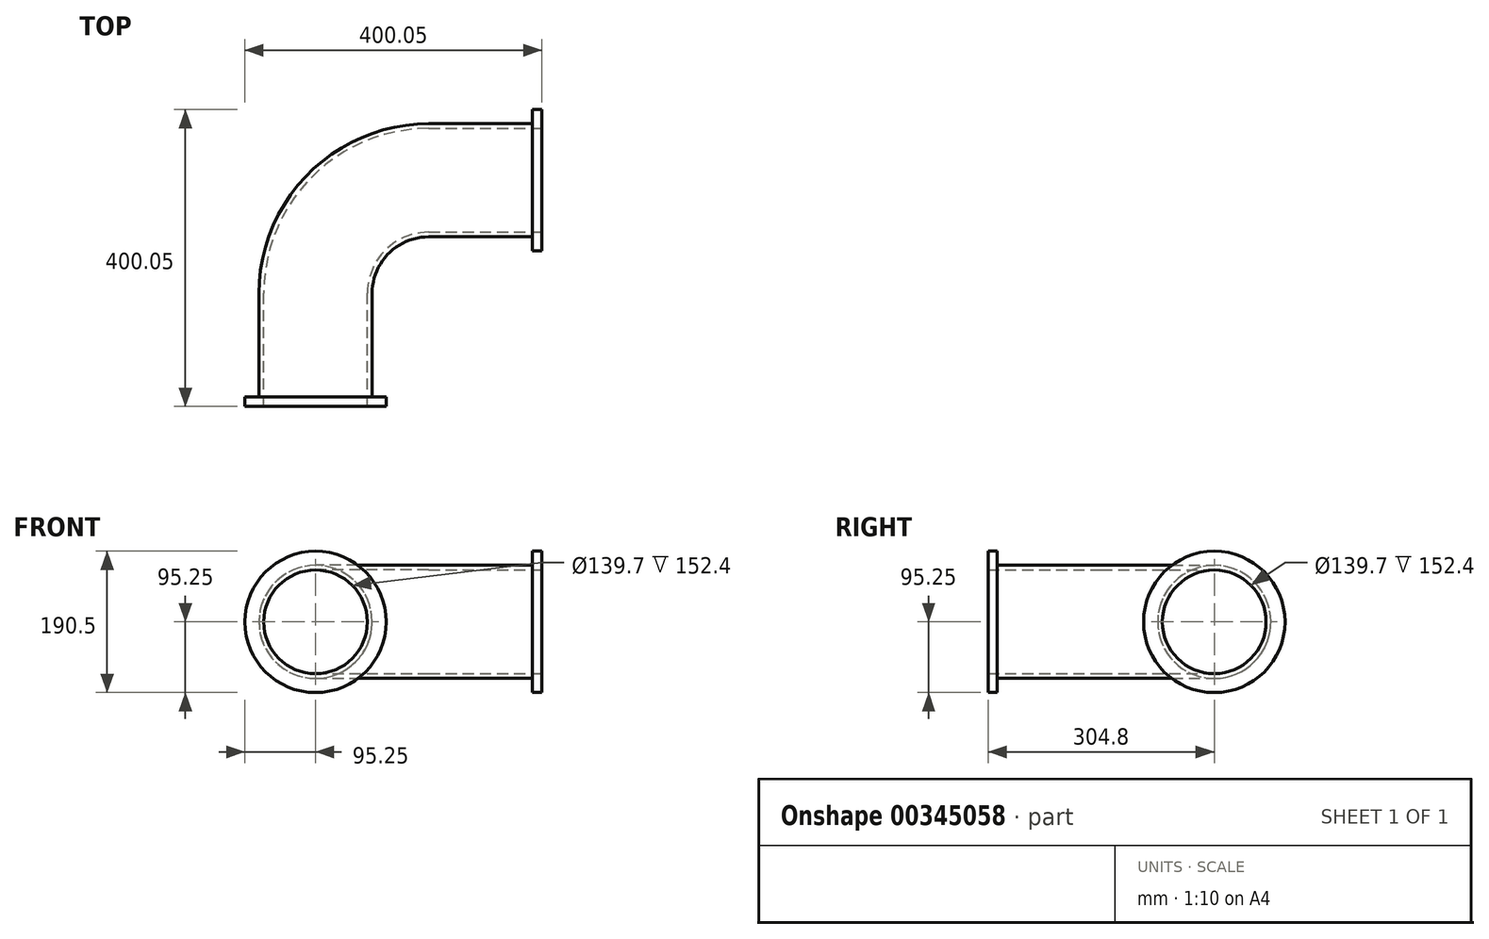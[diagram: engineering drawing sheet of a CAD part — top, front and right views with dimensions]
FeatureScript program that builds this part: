
annotation { "Feature Type Name" : "Feature", "Feature Type Description" : "" }
export const myFeature = defineFeature(function(context is Context, id is Id, definition is map)
    precondition{}
    {
        {
            var Q0;
            Q0=qCreatedBy(makeId("Front.planeOp"),FACE);
            var sketch = newSketch(context, id + "F0", { "sketchPlane" : qUnion([Q0])});
            skCircle(sketch, "E0", {"center": v(0, 0) * mm, "radius": 76.2 * mm});
            skCircle(sketch, "E1", {"center": v(0, 0) * mm, "radius": 95.25 * mm});
            skSolve(sketch);
        }
        {
            var Q0;
            Q0=qCreatedBy(makeId("Top.planeOp"),FACE);
            var sketch = newSketch(context, id + "F1", { "sketchPlane" : qUnion([Q0])});
            skLineSegment(sketch, "E2", {"start": v(0, 0) * mm, "end": v(0, 152.4) * mm});
            skLineSegment(sketch, "E3", {"start": v(152.4, 304.8) * mm, "end": v(304.8, 304.8) * mm});
            skPoint(sketch, "E4.visualSharp", {"position": v(0, 304.8) * mm});
            skArc(sketch, "E4.filletArc", {"start": v(152.4, 304.8) * mm, "mid": v(44.64, 260.16) * mm, "end": v(0, 152.4) * mm});
            skSolve(sketch);
        }
        {
            var Q0;
            Q0=makeQuery(id+"F0.imprint","IMPRINT",FACE,{"disambiguationData":[TD([[makeQuery(id+"F0.imprint","IMPRINT",EDGE,{"derivedFrom":sQuery(id+"F0.wireOp",EDGE,"E0")}),1.0]])]});
            var Q1;
            Q1=sQuery(id+"F1.wireOp",EDGE,"E2");
            var Q2;
            Q2=sQuery(id+"F1.wireOp",EDGE,"E4.filletArc");
            var Q3;
            Q3=sQuery(id+"F1.wireOp",EDGE,"E3");
            sweep(context, id + "F2", {"profiles" : qUnion([Q0]), "path" : qUnion([Q1, Q2, Q3])});
        }
        {
            var Q0;
            Q0=makeQuery(id+"F2.opSweep","CAP_FACE",FACE,{"disambiguationData":[OSD([sQuery(id+"F0.wireOp",EDGE,"E0"),sQuery(id+"F1.wireOp",VERTEX,"E2.start")])],"isStart":true});
            var Q1;
            Q1=makeQuery(id+"F2.opSweep","CAP_FACE",FACE,{"disambiguationData":[OSD([sQuery(id+"F0.wireOp",EDGE,"E0"),sQuery(id+"F1.wireOp",VERTEX,"E3.end")])],"isStart":false});
            var Q2;
            Q2=makeQuery(id+"F2.opSweep","SWEPT_BODY",BODY,{"disambiguationData":[OSD([sQuery(id+"F0.wireOp",EDGE,"E0"),sQuery(id+"F1.wireOp",EDGE,"E3")])]});
            shell(context, id + "F3", {"entities" : qUnion([Q0, Q1]), "parts" : qUnion([Q2]), "thickness" : 6.35 * mm});
        }
        {
            var Q0;
            Q0=makeQuery(id+"F0.imprint","IMPRINT",FACE,{"disambiguationData":[TD([[makeQuery(id+"F0.imprint","IMPRINT",EDGE,{"derivedFrom":sQuery(id+"F0.wireOp",EDGE,"E0")}),-1.0]])]});
            extrude(context, id + "F4", {"entities" : qUnion([Q0]), "operationType" : NewBodyOperationType.ADD, "depth" : -12.7 * mm});
        }
        {
            var Q0;
            Q0=sQuery(id+"F1.wireOp",EDGE,"E3");
            var Q1;
            Q1=sQuery(id+"F1.wireOp",VERTEX,"E3.end");
            cPlane(context, id + "F5", {"entities" : qUnion([Q0, Q1]), "cplaneType" : CPlaneType.LINE_POINT, "offset" : 25.4 * mm, "width" : 152.4 * mm, "height" : 152.4 * mm});
        }
        {
            var Q0;
            Q0=qCreatedBy(id+"F5.planeOp",FACE);
            var sketch = newSketch(context, id + "F6", { "sketchPlane" : qUnion([Q0])});
            skCircle(sketch, "E5", {"center": v(304.8, 0) * mm, "radius": 76.2 * mm});
            skCircle(sketch, "E6", {"center": v(304.8, 0) * mm, "radius": 95.25 * mm});
            skSolve(sketch);
        }
        {
            var Q0;
            Q0=makeQuery(id+"F6.imprint","IMPRINT",FACE,{"disambiguationData":[TD([[makeQuery(id+"F6.imprint","IMPRINT",EDGE,{"derivedFrom":sQuery(id+"F6.wireOp",EDGE,"E5")}),-1.0]])]});
            extrude(context, id + "F7", {"entities" : qUnion([Q0]), "operationType" : NewBodyOperationType.ADD, "depth" : -12.7 * mm});
        }
    });
